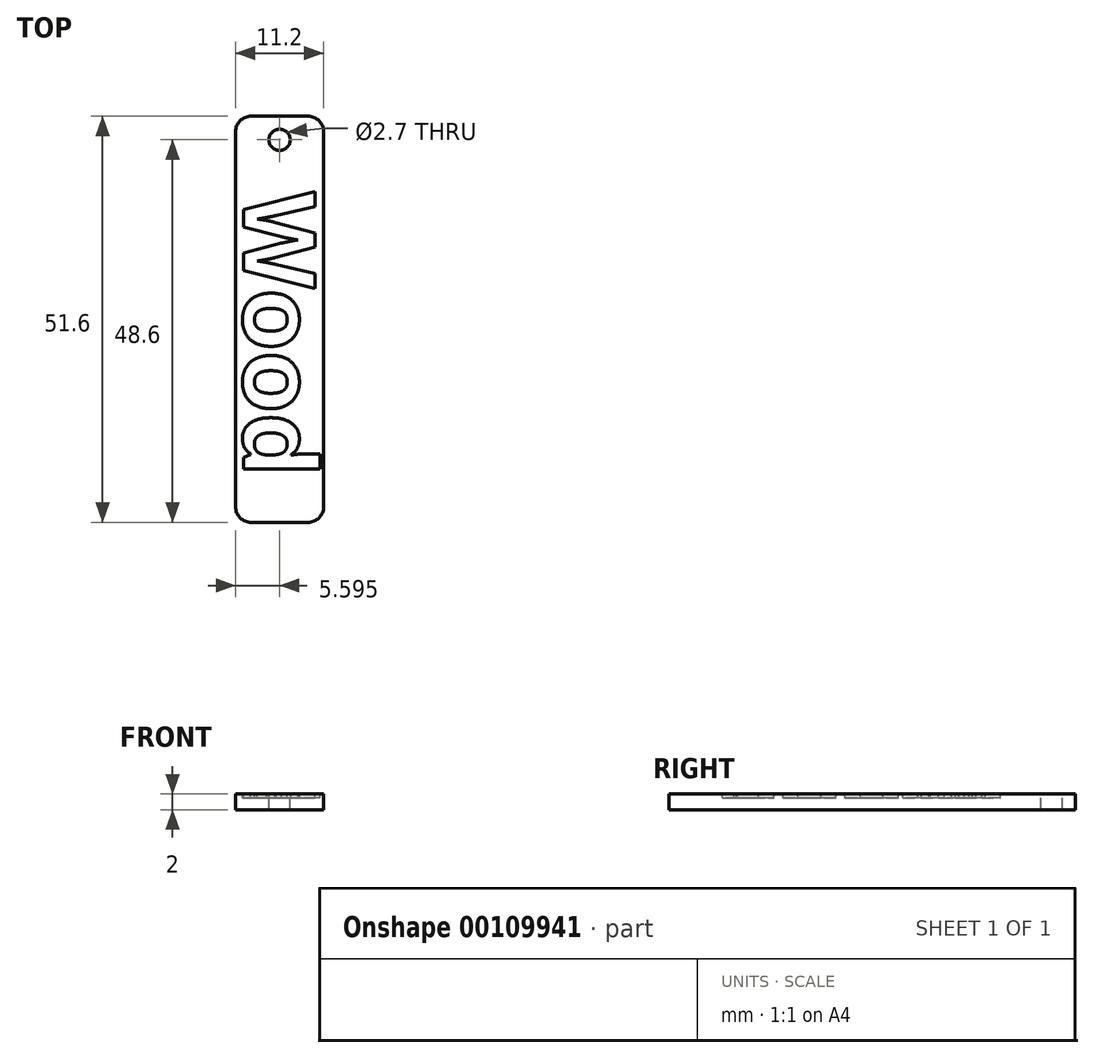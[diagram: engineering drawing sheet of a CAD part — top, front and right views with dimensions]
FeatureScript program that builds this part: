
annotation { "Feature Type Name" : "Feature", "Feature Type Description" : "" }
export const myFeature = defineFeature(function(context is Context, id is Id, definition is map)
    precondition{}
    {
        {
            var Q0;
            Q0=qCreatedBy(makeId("Top.planeOp"),FACE);
            var sketch = newSketch(context, id + "F0", { "sketchPlane" : qUnion([Q0])});
            skLineSegment(sketch, "E0.bottom", {"start": v(-49.26, 74.69) * mm, "end": v(-38.06, 74.69) * mm});
            skLineSegment(sketch, "E0.top", {"start": v(-49.26, 23.09) * mm, "end": v(-38.06, 23.09) * mm});
            skLineSegment(sketch, "E0.left", {"start": v(-49.26, 74.69) * mm, "end": v(-49.26, 23.09) * mm});
            skLineSegment(sketch, "E0.right", {"start": v(-38.06, 74.69) * mm, "end": v(-38.06, 23.09) * mm});
            skCircle(sketch, "E1", {"center": v(-43.66, 71.69) * mm, "radius": 1.35 * mm});
            skText(sketch, "E2", { "text": "Wood", "fontName": "OpenSans-Bold.ttf"});
            const initialGuessF0  = {"E2": [-0.04826, 0.06514, 0, -1, 0.0092]};
            skSetInitialGuess(sketch, initialGuessF0);
            skSolve(sketch);
        }
        {
            var Q0;
            Q0=makeQuery(id+"F0.imprint","IMPRINT",FACE,{"disambiguationData":[TD([[makeQuery(id+"F0.imprint","IMPRINT",EDGE,{"derivedFrom":sQuery(id+"F0.wireOp",EDGE,"E2.sketch_text.stroke-8")}),1.0]])]});
            var Q1;
            Q1=makeQuery(id+"F0.imprint","IMPRINT",FACE,{"disambiguationData":[TD([[makeQuery(id+"F0.imprint","IMPRINT",EDGE,{"derivedFrom":sQuery(id+"F0.wireOp",EDGE,"E2.sketch_text.stroke-14")}),-1.0]])]});
            var Q2;
            Q2=makeQuery(id+"F0.imprint","IMPRINT",FACE,{"disambiguationData":[TD([[makeQuery(id+"F0.imprint","IMPRINT",EDGE,{"derivedFrom":sQuery(id+"F0.wireOp",EDGE,"E2.sketch_text.stroke-32")}),-1.0]])]});
            var Q3;
            Q3=makeQuery(id+"F0.imprint","IMPRINT",FACE,{"disambiguationData":[TD([[makeQuery(id+"F0.imprint","IMPRINT",EDGE,{"derivedFrom":sQuery(id+"F0.wireOp",EDGE,"E2.sketch_text.stroke-49")}),-1.0]])]});
            var Q4;
            Q4=makeQuery(id+"F0.imprint","IMPRINT",FACE,{"disambiguationData":[TD([[makeQuery(id+"F0.imprint","IMPRINT",EDGE,{"derivedFrom":sQuery(id+"F0.wireOp",EDGE,"E2.sketch_text.stroke-69")}),-1.0]])]});
            var Q5;
            Q5=makeQuery(id+"F0.imprint","IMPRINT",FACE,{"disambiguationData":[TD([[makeQuery(id+"F0.imprint","IMPRINT",EDGE,{"derivedFrom":sQuery(id+"F0.wireOp",EDGE,"E0.bottom")}),-1.0]])]});
            var Q6;
            Q6=makeQuery(id+"F0.imprint","IMPRINT",FACE,{"disambiguationData":[TD([[makeQuery(id+"F0.imprint","IMPRINT",EDGE,{"derivedFrom":sQuery(id+"F0.wireOp",EDGE,"E2.sketch_text.stroke-0")}),-1.0]])]});
            var Q7;
            Q7=makeQuery(id+"F0.imprint","IMPRINT",FACE,{"disambiguationData":[TD([[makeQuery(id+"F0.imprint","IMPRINT",EDGE,{"derivedFrom":sQuery(id+"F0.wireOp",EDGE,"E2.sketch_text.stroke-49")}),1.0]])]});
            var Q8;
            Q8=makeQuery(id+"F0.imprint","IMPRINT",FACE,{"disambiguationData":[TD([[makeQuery(id+"F0.imprint","IMPRINT",EDGE,{"derivedFrom":sQuery(id+"F0.wireOp",EDGE,"E2.sketch_text.stroke-24")}),1.0]])]});
            var Q9;
            Q9=makeQuery(id+"F0.imprint","IMPRINT",FACE,{"disambiguationData":[TD([[makeQuery(id+"F0.imprint","IMPRINT",EDGE,{"derivedFrom":sQuery(id+"F0.wireOp",EDGE,"E2.sketch_text.stroke-74")}),1.0]])]});
            extrude(context, id + "F1", {"entities" : qUnion([Q0, Q1, Q2, Q3, Q4, Q5, Q6, Q7, Q8, Q9]), "oppositeDirection" : true, "depth" : 2 * mm});
        }
        {
            var Q0;
            Q0=makeQuery(id+"F0.imprint","IMPRINT",FACE,{"disambiguationData":[TD([[makeQuery(id+"F0.imprint","IMPRINT",EDGE,{"derivedFrom":sQuery(id+"F0.wireOp",EDGE,"E2.sketch_text.stroke-0")}),-1.0]])]});
            var Q1;
            Q1=makeQuery(id+"F0.imprint","IMPRINT",FACE,{"disambiguationData":[TD([[makeQuery(id+"F0.imprint","IMPRINT",EDGE,{"derivedFrom":sQuery(id+"F0.wireOp",EDGE,"E2.sketch_text.stroke-16")}),-1.0]])]});
            var Q2;
            Q2=makeQuery(id+"F0.imprint","IMPRINT",FACE,{"disambiguationData":[TD([[makeQuery(id+"F0.imprint","IMPRINT",EDGE,{"derivedFrom":sQuery(id+"F0.wireOp",EDGE,"E2.sketch_text.stroke-28")}),-1.0]])]});
            var Q3;
            Q3=makeQuery(id+"F0.imprint","IMPRINT",FACE,{"disambiguationData":[TD([[makeQuery(id+"F0.imprint","IMPRINT",EDGE,{"derivedFrom":sQuery(id+"F0.wireOp",EDGE,"E2.sketch_text.stroke-36")}),-1.0]])]});
            var Q4;
            Q4=makeQuery(id+"F0.imprint","IMPRINT",FACE,{"disambiguationData":[TD([[makeQuery(id+"F0.imprint","IMPRINT",EDGE,{"derivedFrom":sQuery(id+"F0.wireOp",EDGE,"E2.sketch_text.stroke-49")}),-1.0]])]});
            var Q5;
            Q5=makeQuery(id+"F0.imprint","IMPRINT",FACE,{"disambiguationData":[TD([[makeQuery(id+"F0.imprint","IMPRINT",EDGE,{"derivedFrom":sQuery(id+"F0.wireOp",EDGE,"E2.sketch_text.stroke-69")}),-1.0]])]});
            var Q6;
            Q6=qConstructionFilter(qBodyType(qCreatedBy(id+"F0",EDGE),BodyType.WIRE),ConstructionObject.NO);
            extrude(context, id + "F2", {"entities" : qUnion([Q0, Q1, Q2, Q3, Q4, Q5]), "operationType" : NewBodyOperationType.REMOVE, "surfaceEntities" : qUnion([Q6]), "oppositeDirection" : true, "depth" : .5 * mm});
        }
        {
            var Q0;
            Q0=makeQuery(id+"F1.opExtrude","SWEPT_EDGE",EDGE,{"disambiguationData":[OSD([sQuery(id+"F0.wireOp",EDGE,"E0.bottom"),sQuery(id+"F0.wireOp",EDGE,"E0.left")])]});
            var Q1;
            Q1=makeQuery(id+"F1.opExtrude","SWEPT_EDGE",EDGE,{"disambiguationData":[OSD([sQuery(id+"F0.wireOp",EDGE,"E0.bottom"),sQuery(id+"F0.wireOp",EDGE,"E0.right")])]});
            var Q2;
            Q2=makeQuery(id+"F1.opExtrude","SWEPT_EDGE",EDGE,{"disambiguationData":[OSD([sQuery(id+"F0.wireOp",EDGE,"E0.top"),sQuery(id+"F0.wireOp",EDGE,"E0.right")])]});
            var Q3;
            Q3=makeQuery(id+"F1.opExtrude","SWEPT_EDGE",EDGE,{"disambiguationData":[OSD([sQuery(id+"F0.wireOp",EDGE,"E0.top"),sQuery(id+"F0.wireOp",EDGE,"E0.left")])]});
            fillet(context, id + "F3", {"entities" : qUnion([Q0, Q1, Q2, Q3]), "radius" : 2 * mm, "tangentPropagation" : true, "allowEdgeOverflow" : false});
        }
    });
